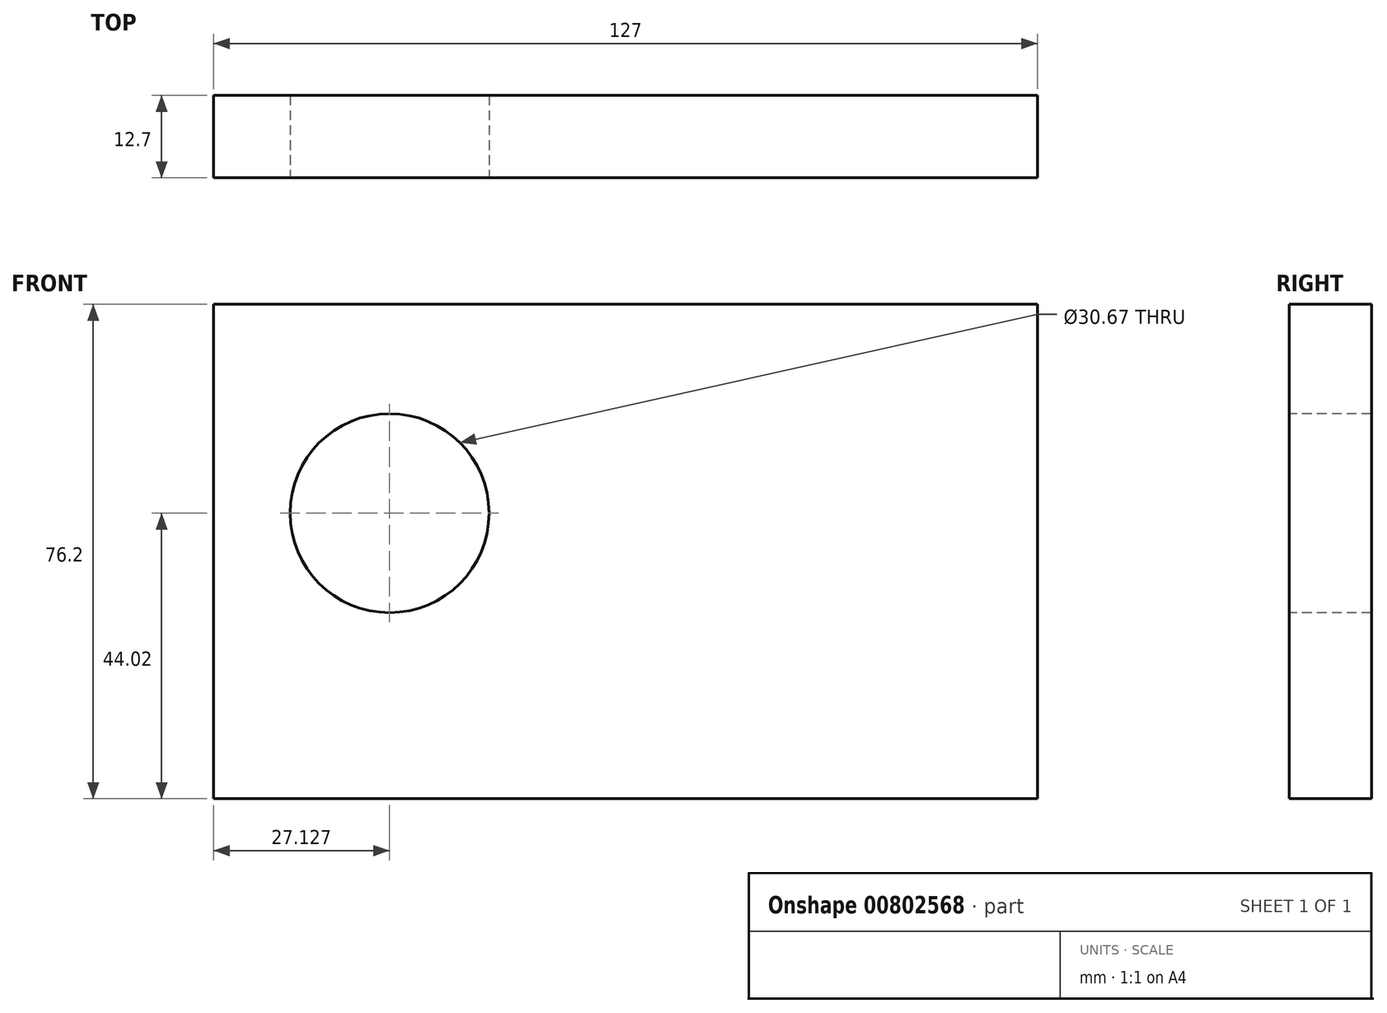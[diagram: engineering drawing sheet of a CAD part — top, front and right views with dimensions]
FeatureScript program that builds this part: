
annotation { "Feature Type Name" : "Feature", "Feature Type Description" : "" }
export const myFeature = defineFeature(function(context is Context, id is Id, definition is map)
    precondition{}
    {
        {
            var Q0;
            Q0=qCreatedBy(makeId("Front.planeOp"),FACE);
            var sketch = newSketch(context, id + "F0", { "sketchPlane" : qUnion([Q0])});
            skLineSegment(sketch, "E0", {"start": v(-69.34, 37.52) * mm, "end": v(-69.34, -38.68) * mm});
            skLineSegment(sketch, "E1", {"start": v(57.66, -38.68) * mm, "end": v(57.66, 37.52) * mm});
            skLineSegment(sketch, "E2", {"start": v(57.66, 37.52) * mm, "end": v(-69.34, 37.52) * mm});
            skLineSegment(sketch, "E3", {"start": v(-69.34, -38.68) * mm, "end": v(57.66, -38.68) * mm});
            skSolve(sketch);
        }
        {
            var Q0;
            Q0=makeQuery(id+"F0.imprint","IMPRINT",FACE,{"disambiguationData":[TD([[makeQuery(id+"F0.imprint","IMPRINT",EDGE,{"derivedFrom":sQuery(id+"F0.wireOp",EDGE,"E0")}),1.0]])]});
            extrude(context, id + "F1", {"entities" : qUnion([Q0]), "depth" : 12.7 * mm, "offsetDistance" : 25.4 * mm});
        }
        {
            var Q0;
            Q0=makeQuery(id+"F1.opExtrude","CAP_FACE",FACE,{"disambiguationData":[OSD([sQuery(id+"F0.wireOp",EDGE,"E0"),sQuery(id+"F0.wireOp",EDGE,"E1"),sQuery(id+"F0.wireOp",EDGE,"E2"),sQuery(id+"F0.wireOp",EDGE,"E3")])],"isStart":false});
            var sketch = newSketch(context, id + "F2", { "sketchPlane" : qUnion([Q0])});
            skSolve(sketch);
        }
        {
            var Q0;
            Q0=makeQuery(id+"F2.imprint","IMPRINT",FACE,{"disambiguationData":[TD([[makeQuery(id+"F2.imprint","IMPRINT",EDGE,{"derivedFrom":makeQuery(id+"F1.opExtrude","CAP_EDGE",EDGE,{"disambiguationData":[OSD([sQuery(id+"F0.wireOp",EDGE,"E0")])],"isStart":false})}),1.0]])]});
            var sketch = newSketch(context, id + "F3", { "sketchPlane" : qUnion([Q0])});
            skCircle(sketch, "E4", {"center": v(-42.21, 5.34) * mm, "radius": 15.34 * mm});
            skSolve(sketch);
        }
        {
            var Q0;
            Q0=makeQuery(id+"F3.imprint","IMPRINT",FACE,{"disambiguationData":[TD([[makeQuery(id+"F3.imprint","IMPRINT",EDGE,{"derivedFrom":sQuery(id+"F3.wireOp",EDGE,"E4")}),1.0]])]});
            extrude(context, id + "F4", {"entities" : qUnion([Q0]), "operationType" : NewBodyOperationType.REMOVE, "oppositeDirection" : true, "depth" : 25.4 * mm, "offsetDistance" : 25.4 * mm});
        }
    });
